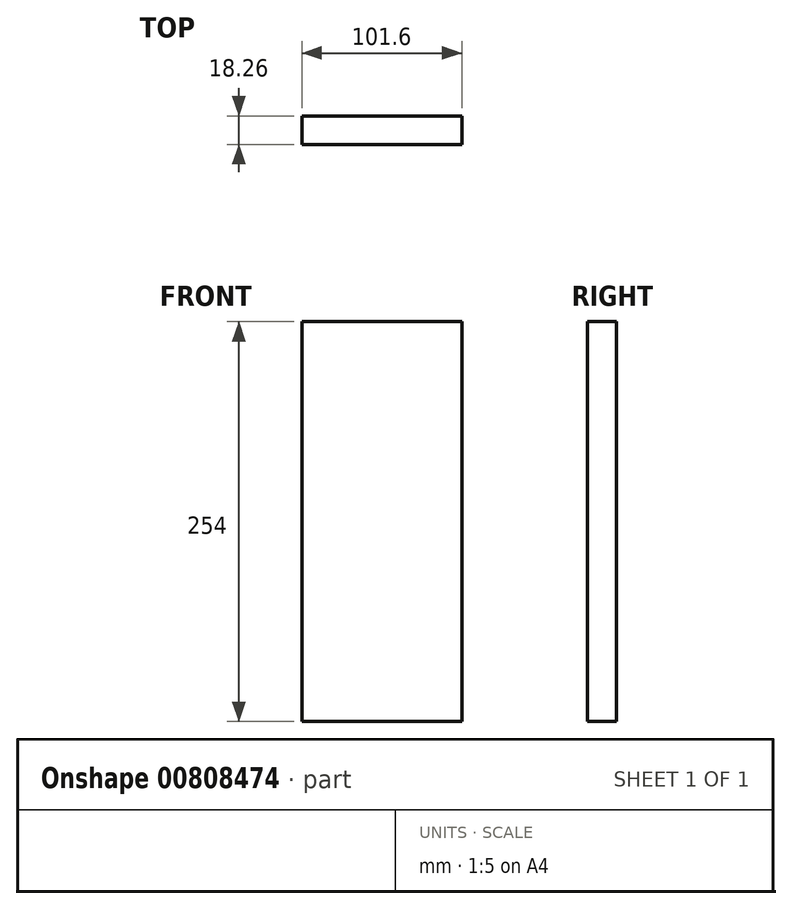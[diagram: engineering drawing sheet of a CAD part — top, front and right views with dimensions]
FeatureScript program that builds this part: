
annotation { "Feature Type Name" : "Feature", "Feature Type Description" : "" }
export const myFeature = defineFeature(function(context is Context, id is Id, definition is map)
    precondition{}
    {
        {
            var Q0;
            Q0=qCreatedBy(makeId("Front.planeOp"),FACE);
            var sketch = newSketch(context, id + "F0", { "sketchPlane" : qUnion([Q0])});
            skLineSegment(sketch, "E0.bottom", {"start": v(50.8, 127) * mm, "end": v(-50.8, 127) * mm});
            skLineSegment(sketch, "E0.top", {"start": v(50.8, -127) * mm, "end": v(-50.8, -127) * mm});
            skLineSegment(sketch, "E0.left", {"start": v(50.8, 127) * mm, "end": v(50.8, -127) * mm});
            skLineSegment(sketch, "E0.right", {"start": v(-50.8, 127) * mm, "end": v(-50.8, -127) * mm});
            skPoint(sketch, "E0.middle", {"position": v(0, 0) * mm});
            skSolve(sketch);
        }
        {
            var Q0;
            Q0 = qSketchRegion(id + "F0", true);
            extrude(context, id + "F1", {"entities" : qUnion([Q0]), "depth" : 18.26 * mm, "offsetDistance" : 25.4 * mm});
        }
    });
